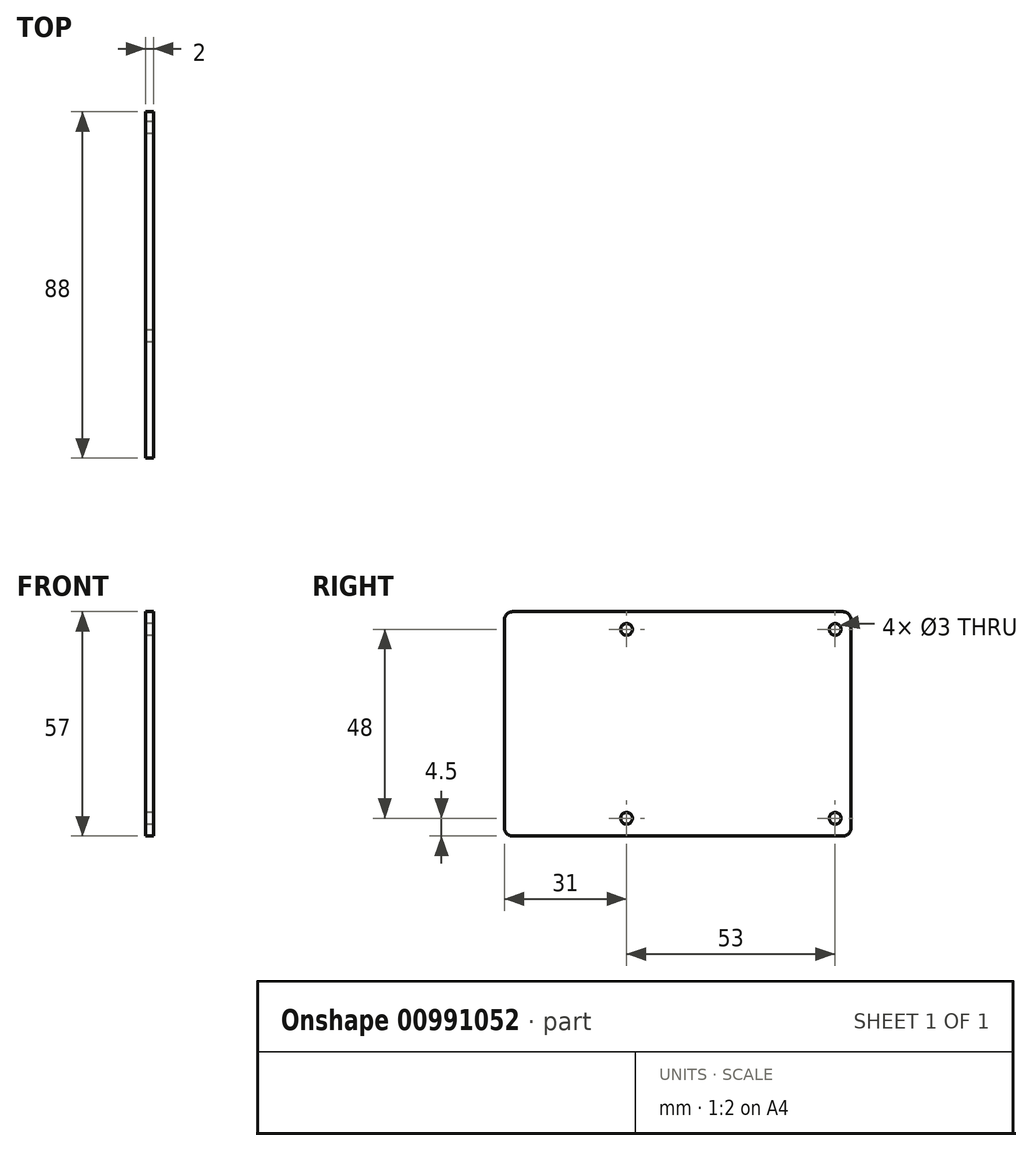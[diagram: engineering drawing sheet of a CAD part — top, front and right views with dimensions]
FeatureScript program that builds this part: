
annotation { "Feature Type Name" : "Feature", "Feature Type Description" : "" }
export const myFeature = defineFeature(function(context is Context, id is Id, definition is map)
    precondition{}
    {
        {
            var Q0;
            Q0=qCreatedBy(makeId("Right.planeOp"),FACE);
            var sketch = newSketch(context, id + "F0", { "sketchPlane" : qUnion([Q0])});
            skLineSegment(sketch, "E0.bottom", {"start": v(0, 0) * mm, "end": v(88, 0) * mm});
            skLineSegment(sketch, "E0.top", {"start": v(0, 57) * mm, "end": v(88, 57) * mm});
            skLineSegment(sketch, "E0.left", {"start": v(0, 0) * mm, "end": v(0, 57) * mm});
            skLineSegment(sketch, "E0.right", {"start": v(88, 0) * mm, "end": v(88, 57) * mm});
            skCircle(sketch, "E1", {"center": v(84, 52.5) * mm, "radius": 1.5 * mm});
            skCircle(sketch, "E2", {"center": v(84, 4.5) * mm, "radius": 1.5 * mm});
            skCircle(sketch, "E3", {"center": v(31, 52.5) * mm, "radius": 1.5 * mm});
            skCircle(sketch, "E4", {"center": v(31, 4.5) * mm, "radius": 1.5 * mm});
            skSolve(sketch);
        }
        {
            var Q0;
            Q0=makeQuery(id+"F0.imprint","IMPRINT",FACE,{"disambiguationData":[TD([[makeQuery(id+"F0.imprint","IMPRINT",EDGE,{"derivedFrom":sQuery(id+"F0.wireOp",EDGE,"E0.bottom")}),1.0]])]});
            extrude(context, id + "F1", {"entities" : qUnion([Q0]), "depth" : 2 * mm, "offsetDistance" : 25 * mm});
        }
        {
            var Q0;
            Q0=makeQuery(id+"F1.opExtrude","SWEPT_EDGE",EDGE,{"disambiguationData":[OSD([sQuery(id+"F0.wireOp",EDGE,"E0.bottom"),sQuery(id+"F0.wireOp",EDGE,"E0.left")])]});
            var Q1;
            Q1=makeQuery(id+"F1.opExtrude","SWEPT_EDGE",EDGE,{"disambiguationData":[OSD([sQuery(id+"F0.wireOp",EDGE,"E0.bottom"),sQuery(id+"F0.wireOp",EDGE,"E0.right")])]});
            var Q2;
            Q2=makeQuery(id+"F1.opExtrude","SWEPT_EDGE",EDGE,{"disambiguationData":[OSD([sQuery(id+"F0.wireOp",EDGE,"E0.top"),sQuery(id+"F0.wireOp",EDGE,"E0.left")])]});
            var Q3;
            Q3=makeQuery(id+"F1.opExtrude","SWEPT_EDGE",EDGE,{"disambiguationData":[OSD([sQuery(id+"F0.wireOp",EDGE,"E0.top"),sQuery(id+"F0.wireOp",EDGE,"E0.right")])]});
            fillet(context, id + "F2", {"entities" : qUnion([Q0, Q1, Q2, Q3]), "radius" : 2 * mm, "tangentPropagation" : true, "allowEdgeOverflow" : false});
        }
    });
